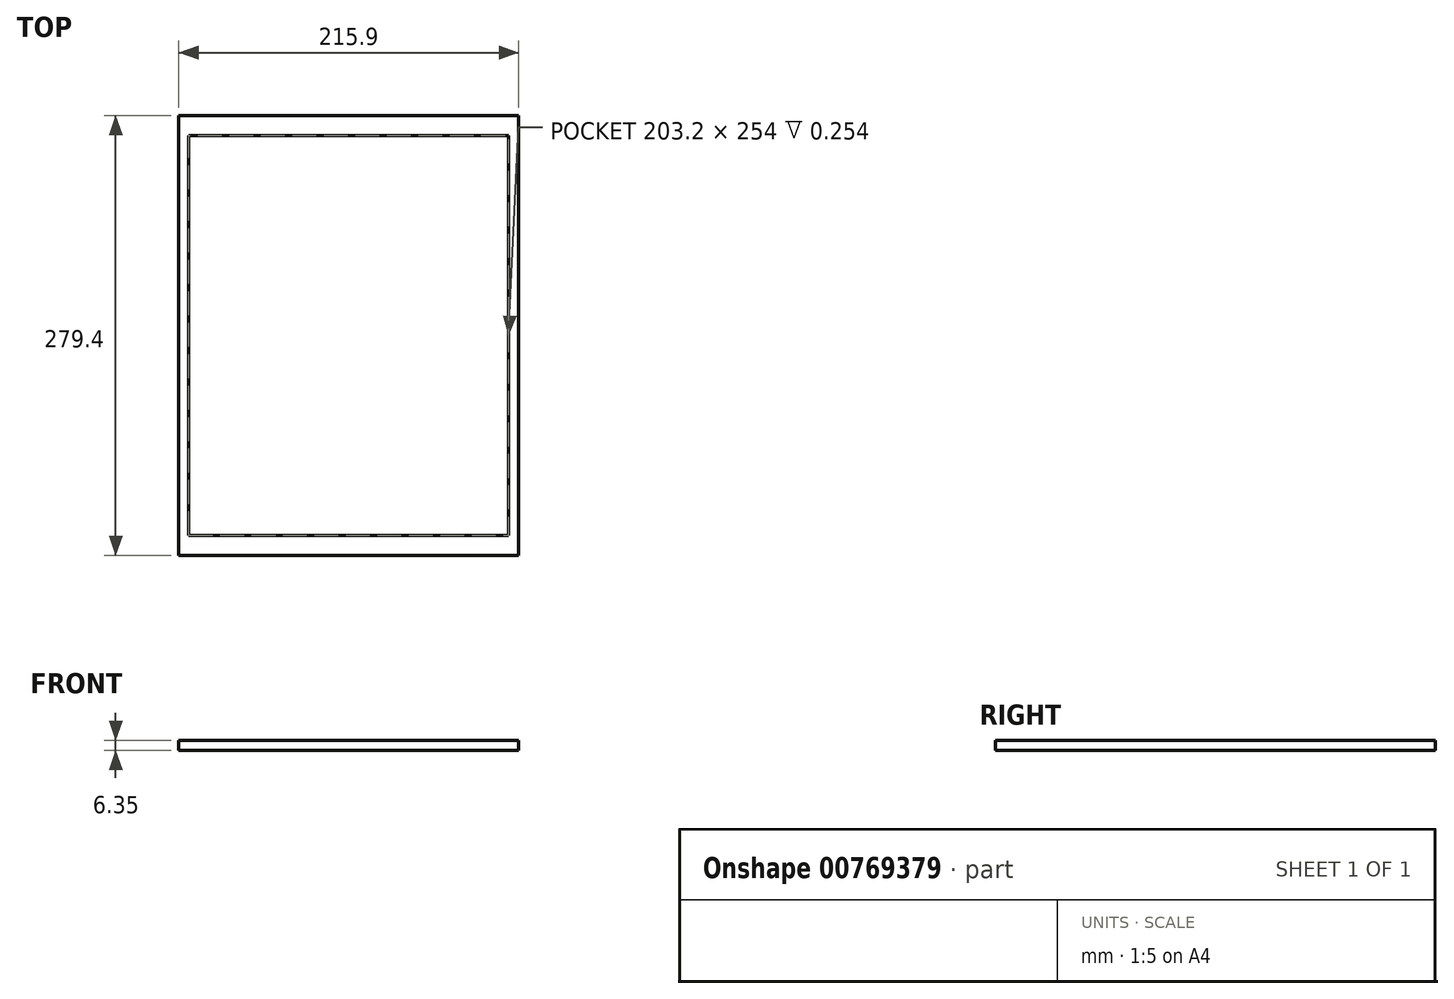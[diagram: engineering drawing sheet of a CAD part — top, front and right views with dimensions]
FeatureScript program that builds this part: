
annotation { "Feature Type Name" : "Feature", "Feature Type Description" : "" }
export const myFeature = defineFeature(function(context is Context, id is Id, definition is map)
    precondition{}
    {
        {
            var Q0;
            Q0=qCreatedBy(makeId("Top.planeOp"),FACE);
            var sketch = newSketch(context, id + "F0", { "sketchPlane" : qUnion([Q0])});
            skLineSegment(sketch, "E0.bottom", {"start": v(107.95, -139.7) * mm, "end": v(-107.95, -139.7) * mm});
            skLineSegment(sketch, "E0.top", {"start": v(107.95, 139.7) * mm, "end": v(-107.95, 139.7) * mm});
            skLineSegment(sketch, "E0.left", {"start": v(107.95, -139.7) * mm, "end": v(107.95, 139.7) * mm});
            skLineSegment(sketch, "E0.right", {"start": v(-107.95, -139.7) * mm, "end": v(-107.95, 139.7) * mm});
            skPoint(sketch, "E0.middle", {"position": v(0, 0) * mm});
            skSolve(sketch);
        }
        {
            var Q0;
            Q0=makeQuery(id+"F0.imprint","IMPRINT",FACE,{"disambiguationData":[TD([[makeQuery(id+"F0.imprint","IMPRINT",EDGE,{"derivedFrom":sQuery(id+"F0.wireOp",EDGE,"E0.bottom")}),-1.0]])]});
            extrude(context, id + "F1", {"entities" : qUnion([Q0]), "depth" : 6.35 * mm, "offsetDistance" : 25.4 * mm});
        }
        {
            var Q0;
            Q0=makeQuery(id+"F1.opExtrude","CAP_FACE",FACE,{"disambiguationData":[OSD([sQuery(id+"F0.wireOp",EDGE,"E0.bottom"),sQuery(id+"F0.wireOp",EDGE,"E0.top"),sQuery(id+"F0.wireOp",EDGE,"E0.left"),sQuery(id+"F0.wireOp",EDGE,"E0.right")])],"isStart":false});
            var sketch = newSketch(context, id + "F2", { "sketchPlane" : qUnion([Q0])});
            skLineSegment(sketch, "E1.bottom", {"start": v(101.6, -127) * mm, "end": v(-101.6, -127) * mm});
            skLineSegment(sketch, "E1.top", {"start": v(101.6, 127) * mm, "end": v(-101.6, 127) * mm});
            skLineSegment(sketch, "E1.left", {"start": v(101.6, -127) * mm, "end": v(101.6, 127) * mm});
            skLineSegment(sketch, "E1.right", {"start": v(-101.6, -127) * mm, "end": v(-101.6, 127) * mm});
            skPoint(sketch, "E1.middle", {"position": v(0, 0) * mm});
            skSolve(sketch);
        }
        {
            var Q0;
            Q0 = qSketchRegion(id + "F2", true);
            extrude(context, id + "F3", {"entities" : qUnion([Q0]), "operationType" : NewBodyOperationType.REMOVE, "oppositeDirection" : true, "depth" : 0.25 * mm, "offsetDistance" : 25.4 * mm});
        }
    });
